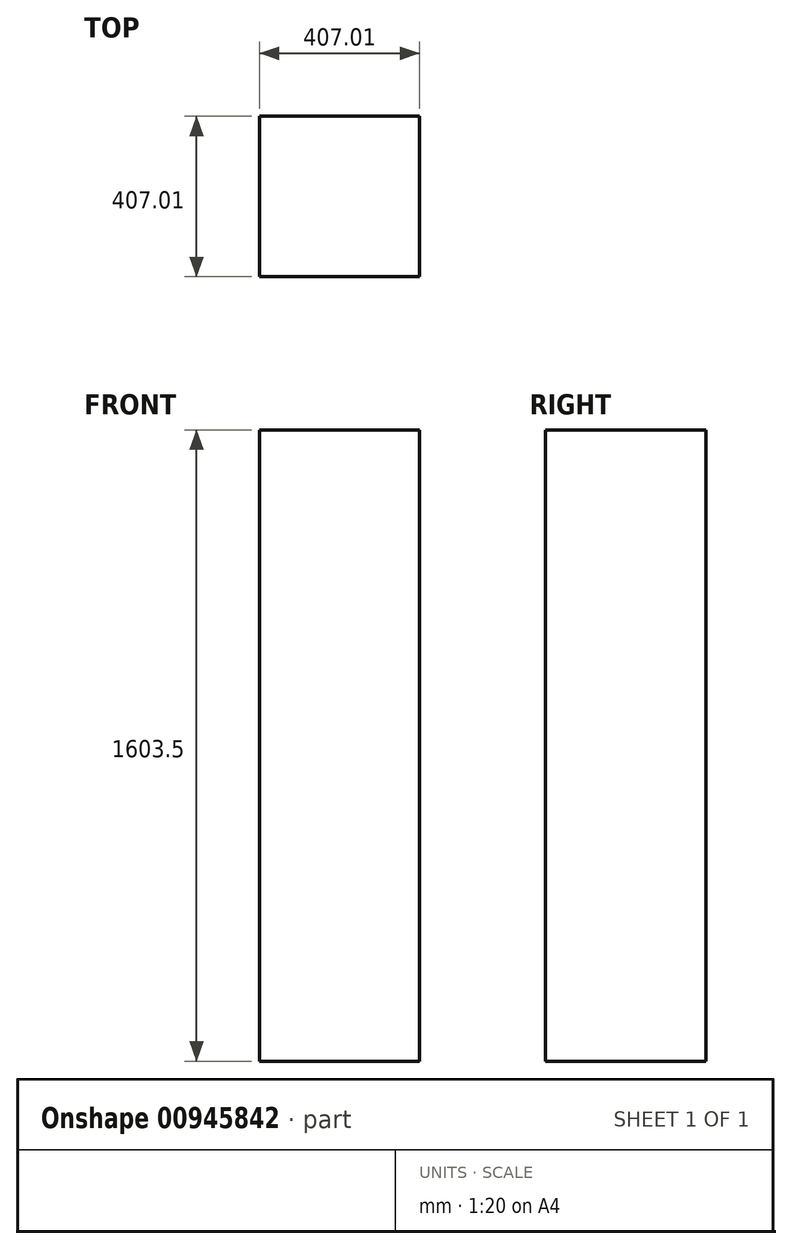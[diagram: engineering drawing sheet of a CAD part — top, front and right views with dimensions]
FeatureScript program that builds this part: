
annotation { "Feature Type Name" : "Feature", "Feature Type Description" : "" }
export const myFeature = defineFeature(function(context is Context, id is Id, definition is map)
    precondition{}
    {
        {
            var Q0;
            Q0=qCreatedBy(makeId("Top.planeOp"),FACE);
            var sketch = newSketch(context, id + "F0", { "sketchPlane" : qUnion([Q0])});
            skLineSegment(sketch, "E0.bottom", {"start": v(-407, 407) * mm, "end": v(0, 407) * mm});
            skLineSegment(sketch, "E0.top", {"start": v(-407, 0) * mm, "end": v(0, 0) * mm});
            skLineSegment(sketch, "E0.left", {"start": v(-407, 407) * mm, "end": v(-407, 0) * mm});
            skLineSegment(sketch, "E0.right", {"start": v(0, 407) * mm, "end": v(0, 0) * mm});
            skSolve(sketch);
        }
        {
            var Q0;
            Q0=makeQuery(id+"F0.imprint","IMPRINT",FACE,{"disambiguationData":[TD([[makeQuery(id+"F0.imprint","IMPRINT",EDGE,{"derivedFrom":sQuery(id+"F0.wireOp",EDGE,"E0.bottom")}),-1.0]])]});
            extrude(context, id + "F1", {"entities" : qUnion([Q0]), "depth" : 1603.5 * mm, "offsetDistance" : 25.4 * mm});
        }
    });
